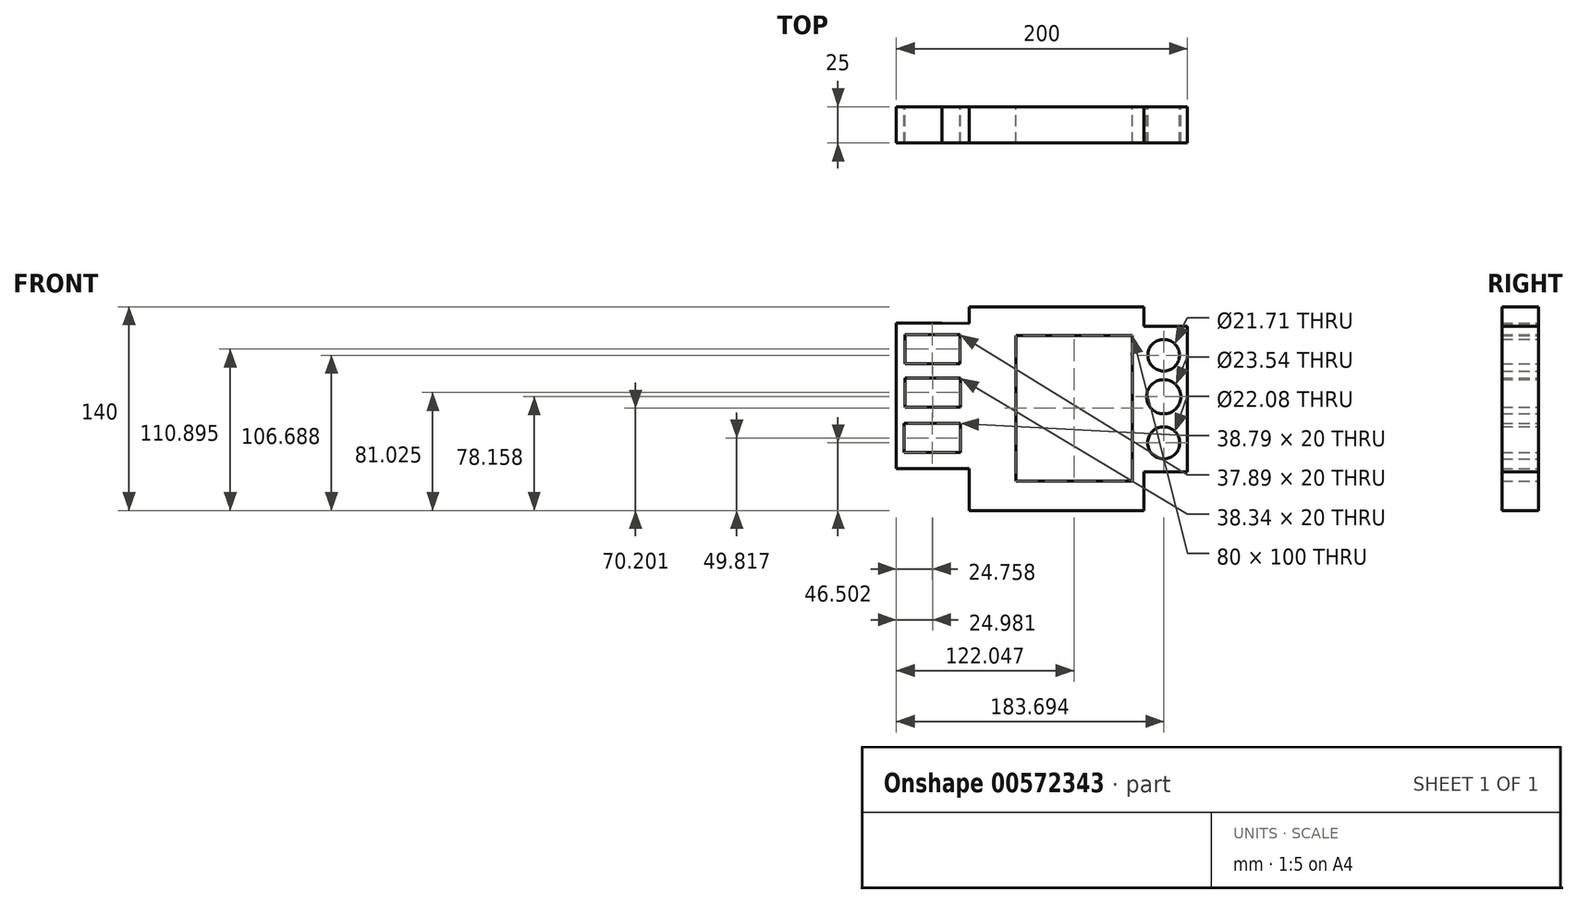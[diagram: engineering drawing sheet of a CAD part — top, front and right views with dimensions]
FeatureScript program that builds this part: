
annotation { "Feature Type Name" : "Feature", "Feature Type Description" : "" }
export const myFeature = defineFeature(function(context is Context, id is Id, definition is map)
    precondition{}
    {
        {
            var Q0;
            Q0=qCreatedBy(makeId("Front.planeOp"),FACE);
            var sketch = newSketch(context, id + "F0", { "sketchPlane" : qUnion([Q0])});
            skLineSegment(sketch, "E0", {"start": v(-80.32, 621.73) * mm, "end": v(39.68, 621.73) * mm});
            skLineSegment(sketch, "E1", {"start": v(39.68, 620.07) * mm, "end": v(39.68, 621.73) * mm});
            skPoint(sketch, "E2.end.orphan", {"position": v(-80.32, 802) * mm});
            skPoint(sketch, "E3.end.orphan", {"position": v(-176.79, 620.07) * mm});
            skLineSegment(sketch, "E4", {"start": v(-99.02, 750.44) * mm, "end": v(-130.32, 750.44) * mm});
            skLineSegment(sketch, "E5", {"start": v(-130.32, 750.44) * mm, "end": v(-130.32, 650.44) * mm});
            skLineSegment(sketch, "E6", {"start": v(-130.32, 650.44) * mm, "end": v(-80.32, 650.44) * mm});
            skLineSegment(sketch, "E7", {"start": v(69.68, 748.4) * mm, "end": v(39.68, 748.4) * mm});
            skLineSegment(sketch, "E8", {"start": v(39.68, 748.4) * mm, "end": v(39.68, 761.73) * mm});
            skLineSegment(sketch, "E9", {"start": v(39.68, 761.73) * mm, "end": v(-80.32, 761.73) * mm});
            skPoint(sketch, "E10.start.orphan", {"position": v(69.68, 620.07) * mm});
            skLineSegment(sketch, "E11", {"start": v(39.68, 621.73) * mm, "end": v(39.68, 648.4) * mm});
            skLineSegment(sketch, "E12", {"start": v(39.68, 648.4) * mm, "end": v(69.68, 648.4) * mm});
            skLineSegment(sketch, "E13", {"start": v(69.68, 648.4) * mm, "end": v(69.68, 748.4) * mm});
            skLineSegment(sketch, "E14", {"start": v(-80.32, 750.18) * mm, "end": v(-99.02, 750.44) * mm});
            skPoint(sketch, "E15.start.orphan", {"position": v(-80.32, 739.69) * mm});
            skLineSegment(sketch, "E16", {"start": v(-80.32, 761.73) * mm, "end": v(-80.32, 750.18) * mm});
            skPoint(sketch, "E17.start.orphan", {"position": v(-80.32, 587.35) * mm});
            skLineSegment(sketch, "E18", {"start": v(-80.32, 621.73) * mm, "end": v(-80.32, 650.44) * mm});
            skPoint(sketch, "E19.end.orphan", {"position": v(-99.02, 650.44) * mm});
            skLineSegment(sketch, "E20.bottom", {"start": v(-48.27, 741.93) * mm, "end": v(31.73, 741.93) * mm});
            skLineSegment(sketch, "E20.top", {"start": v(-48.27, 641.93) * mm, "end": v(31.73, 641.93) * mm});
            skLineSegment(sketch, "E20.left", {"start": v(-48.27, 741.93) * mm, "end": v(-48.27, 641.93) * mm});
            skLineSegment(sketch, "E20.right", {"start": v(31.73, 741.93) * mm, "end": v(31.73, 641.93) * mm});
            skLineSegment(sketch, "E21.bottom", {"start": v(-124.5, 712.75) * mm, "end": v(-86.17, 712.75) * mm});
            skLineSegment(sketch, "E21.top", {"start": v(-124.5, 692.75) * mm, "end": v(-86.17, 692.75) * mm});
            skLineSegment(sketch, "E21.left", {"start": v(-124.5, 712.75) * mm, "end": v(-124.5, 692.75) * mm});
            skLineSegment(sketch, "E21.right", {"start": v(-86.17, 712.75) * mm, "end": v(-86.17, 692.75) * mm});
            skPoint(sketch, "E22.firstSnap0", {"position": v(-124.5, 702.75) * mm});
            skLineSegment(sketch, "E22.bottom", {"start": v(-124.5, 742.63) * mm, "end": v(-86.61, 742.63) * mm});
            skLineSegment(sketch, "E22.top", {"start": v(-124.5, 722.63) * mm, "end": v(-86.61, 722.63) * mm});
            skLineSegment(sketch, "E22.left", {"start": v(-124.5, 742.63) * mm, "end": v(-124.5, 722.63) * mm});
            skLineSegment(sketch, "E22.right", {"start": v(-86.61, 742.63) * mm, "end": v(-86.61, 722.63) * mm});
            skLineSegment(sketch, "E23.bottom", {"start": v(-124.95, 681.55) * mm, "end": v(-86.17, 681.55) * mm});
            skLineSegment(sketch, "E23.top", {"start": v(-124.95, 661.55) * mm, "end": v(-86.17, 661.55) * mm});
            skLineSegment(sketch, "E23.left", {"start": v(-124.95, 681.55) * mm, "end": v(-124.95, 661.55) * mm});
            skLineSegment(sketch, "E23.right", {"start": v(-86.17, 681.55) * mm, "end": v(-86.17, 661.55) * mm});
            skCircle(sketch, "E24", {"center": v(53.37, 728.42) * mm, "radius": 10.86 * mm});
            skCircle(sketch, "E25", {"center": v(53.37, 699.89) * mm, "radius": 11.77 * mm});
            skCircle(sketch, "E26", {"center": v(53.37, 668.23) * mm, "radius": 11.04 * mm});
            skSolve(sketch);
        }
        {
            var Q0;
            Q0 = qSketchRegion(id + "F0", true);
            extrude(context, id + "F1", {"entities" : qUnion([Q0]), "depth" : 25 * mm, "offsetDistance" : 25 * mm});
        }
    });
